# Revit family: Geberit Alpha gömme rezervuar 8 cm, 6 _ 3 litre_PRO_168865
name_source: partatom
category: Plumbing Fixtures
units: mm (PartAtom-declared; Revit-internal decimal feet)

## family parameters
Always vertical = Yes
Cut with Voids When Loaded = No
OmniClass Number = 23.31.19.00
Part Type = Normal
Room Calculation Point = Yes
Round Connector Dimension = Use Diameter
Shared = No
Work Plane-Based = No

## types (1)
- 109.175.00.1 Geberit Alpha gömme rezervuar 8 cm, 6 / 3 litre
    Application purposes = Tuğla duvarlar için
Yarım veya oda yüksekliğinde duvar önü montaj için
Oda yüksekliğinde alçıpanlara montaj için
Yere oturan klozetler için
2 kademeli deşarj için
    Application range = sanitary systems
    Article number key = 109.175.00.1
    B = 410 mm  [stored 1.34514 ft]
    BIM Content Version = GEB MG 1.6
    BIM Content revision date = 2023.07.05
    Brand = Geberit
    Büyük yıkama miktarı ayar aralığı (l) = 4 / 4.5 / 6 / 7.5 l
    CW Connection = Yes
    Characteristics = Önden basmalı gömme rezervuar
Yoğuşmaya karşı izolasyonlu gömme rezervuar
Sıva taşıyıcı doku önceden monte edilmiştir
Fabrika ayarında hızlı ilave drenaj mümkündür
Geçmeli rezervuar dirseği
Rezervuar dirseği yukarı yönde 2 cm ve aşağı yönde 1 cm ayarlanabilir
Su bağlantısı üstte solda
Servis açıklığı şablon kutusu kısaltılabilir
    Connection description 1 = cold water in
    Connection description 2 = sanitary out
    D1 = 60 mm  [stored 0.19685 ft]
    Default Elevation = 0 mm  [stored 0 ft]
    Description = Geberit Alpha gömme rezervuar 8 cm, 6 / 3 litre
    EAN code basic data = 4025416351825
    GEB_culture = tr-TR
    GEB_generic_description = concealed cistern for toilet
    GEB_generic_manufacturer = generic
    GEB_imperial_engineering = No
    GEB_metric_engineering = Yes
    GEB_pimversion = 23.08.11
    GEB_processing_type = T
    GEB_reference = PRO_168865
    GEB_translations = {"application_range":"Application range","applicationPurposes":"Application purposes","ATT_10673":"EAN code basic data","ATT_10773":"Çalışma basıncı","ATT_10807":"Büyük yıkama miktarı ayar aralığı (l)","ATT_10811":"Küçük yıkama miktarı ayar aralığı","ATT_10866":"Yıkama miktarı fabrika ayarı","brandName":"Brand","characteristics":"Characteristics","connection_description1":"Connection description 1","connection_description2":"Connection description 2","connection_type_c01":"Connection type at connection 01","connection_type_c02":"Connection type at connection 02","content_creator":"BIM Content creator","content_date_changed":"BIM Content revision date","content_version":"BIM Content Version","GEB_connection_diameter1":"Connection diameter 1","GEB_connection_diameter2":"Connection diameter 2","key 1000":"Article number key","name":"Name","productBrand":"Product brand","scopeOfDelivery":"Scope of delivery","type":"Type","GEB_cut_length_c01":"Max cutting length at connection 01","angle":"Angle","placement finished floor":"On Finished Floor Level","sanitary socket":"Adapter socket","surface height":"Thickness of finished floor","warning":"Warning","fixed_material":"Main material","fixed_material_01":"Main material 01","fixed_material_03":"Main material 03","ATT_10931":"B","ATT_10951":"H","ATT_380239":"T"}
    GEB_use_DN = Yes
    H = 615 mm  [stored 2.01772 ft]
    HW Connection = No
    IfcDescription = Geberit Alpha gömme rezervuar 8 cm, 6 / 3 litre
    IfcExportAs = IfcSanitaryTerminal
    IfcExportType = CISTERN
    Küçük yıkama miktarı ayar aralığı = 2-4 l
    LOD300 = No
    LOD400 = Yes
    Main material = Geberit, Plastic, Opaque white
    Main material 01 = Geberit, Laminate, Ivory, Matte
    Main material 03 = Geberit, PE-HD, Black
    Manufacturer = Geberit
    Model = Alpha 8 cm
    Name = Geberit Alpha gömme rezervuar 8 cm, 6 / 3 litre
    Scope of delivery = Su bağlantısı R 1/2", MF uyumlu, entegre ara musluklu ve el volanlı
Servis açıklığı için şablon kutusu
Girinti çanaklı rezervuar dirseği
Rezervuar dirseği uzatması ø 45 mm
Koruyucu tapa
2 sabitleme rayı
2 sabitleme pabucu
Sabitleme malzemesi
    T = 80 mm  [stored 0.262467 ft]
    Type = Alpha 8 cm
    Vent Connection = No
    Waste Connection = Yes
    Yıkama miktarı fabrika ayarı = 6 ve 3 l
    cistern_bottom = 615 mm  [stored 2.01772 ft]
    cistern_depth = 80 mm  [stored 0.262467 ft]
    cistern_top_offset = 0 mm  [stored 0 ft]
    cistern_width = 410 mm  [stored 1.34514 ft]
    connection_bend = No
    flushing_water_pipe_D = 80 mm  [stored 0.262467 ft]
    outlet_flow = 0.0 L/s
    plastering_netting = Yes
    Çalışma basıncı = 0.1-10 bar

note: [stored X ft] marks values corroborated as IEEE doubles in the binary element streams (Revit-internal decimal feet)

## geometry (parser evidence)
native form markers: Blend x4, Sweep x6
no freeform markers — native parametric forms only
